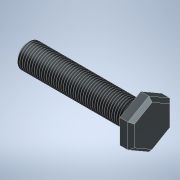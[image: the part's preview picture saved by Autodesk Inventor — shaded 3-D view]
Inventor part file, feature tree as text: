
AUTODESK INVENTOR PART (.ipt)
format: ipt  version: 2021 (Build 250183000, 183)  size: 127,488 bytes
history: native  units: mm
features: sketch x3, extrude x2, chamfer x2, thread x1
ambient origin geometry x8: Origin, YZ Plane, XZ Plane, XY Plane, X Axis, Y Axis, Z Axis, Center Point
bodies: Solid1 (feature_tree)
feature tree (8):
  extrude  "Extrusion1"  Depth=70.0mm TaperAngle=0.0deg
  extrude  "Extrusion2"  Depth=25.91503mm TaperAngle=45.0deg
  chamfer  "Chamfer1"  Distance=54.0mm
  sketch  "Sketch3"  dims[d13=14.96205mm d14=2.0mm d15=2.0mm d16=45.0deg]
  thread  "Thread2"  [1 undecoded]
  chamfer  "Chamfer2"  Distance=2.0mm Angle=45.0deg
  sketch  "Sketch1"  dims[d0=14.9mm d1=70.0mm d2=0.0mm]
  sketch  "Sketch2"  dims[d3=7.0mm d4=0.0mm d5=1.0mm d6=2.0mm d7=45.0deg d10=54.0mm d11=0.0mm d12=25.91503mm]
note: 1 required parameter value undecoded (feature->parameter linkage not recoverable at this tier; creation-order binding heuristic only, values carry confidence <= 0.55)
